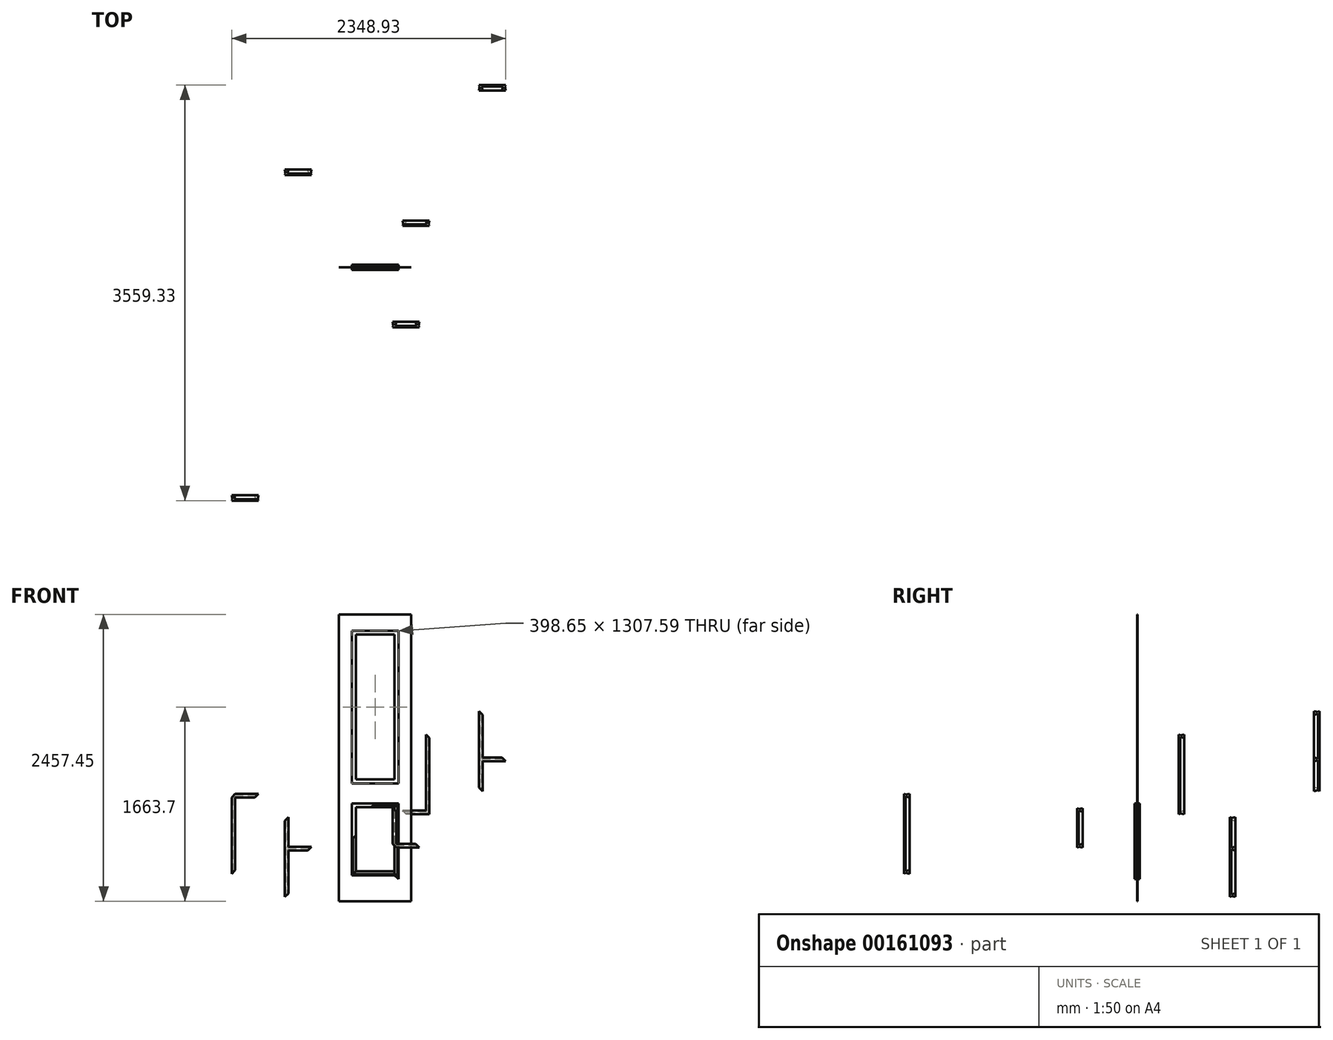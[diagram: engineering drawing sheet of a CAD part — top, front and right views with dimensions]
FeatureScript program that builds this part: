
annotation { "Feature Type Name" : "Feature", "Feature Type Description" : "" }
export const myFeature = defineFeature(function(context is Context, id is Id, definition is map)
    precondition{}
    {
        {
            var Q0;
            Q0=qCreatedBy(makeId("Front.planeOp"),FACE);
            var sketch = newSketch(context, id + "F0", { "sketchPlane" : qUnion([Q0])});
            skLineSegment(sketch, "E0.bottom", {"start": v(0, 0) * mm, "end": v(619.12, 0) * mm});
            skLineSegment(sketch, "E0.top", {"start": v(0, 2457.45) * mm, "end": v(619.12, 2457.45) * mm});
            skLineSegment(sketch, "E0.left", {"start": v(0, 0) * mm, "end": v(0, 2457.45) * mm});
            skLineSegment(sketch, "E0.right", {"start": v(619.12, 0) * mm, "end": v(619.12, 2457.45) * mm});
            skLineSegment(sketch, "E1.bottom", {"start": v(508.89, 2317.5) * mm, "end": v(110.24, 2317.5) * mm});
            skLineSegment(sketch, "E1.top", {"start": v(508.89, 1009.9) * mm, "end": v(110.24, 1009.9) * mm});
            skLineSegment(sketch, "E1.left", {"start": v(508.89, 2317.5) * mm, "end": v(508.89, 1009.9) * mm});
            skLineSegment(sketch, "E1.right", {"start": v(110.24, 2317.5) * mm, "end": v(110.24, 1009.9) * mm});
            skLineSegment(sketch, "E2.bottom", {"start": v(110.24, 837.7) * mm, "end": v(508.89, 837.7) * mm});
            skLineSegment(sketch, "E2.top", {"start": v(110.24, 222.5) * mm, "end": v(508.89, 222.5) * mm});
            skLineSegment(sketch, "E2.left", {"start": v(110.24, 837.7) * mm, "end": v(110.24, 222.5) * mm});
            skLineSegment(sketch, "E2.right", {"start": v(508.89, 837.7) * mm, "end": v(508.89, 222.5) * mm});
            skSolve(sketch);
        }
        {
            var Q0;
            Q0=qSketchRegion(id+"F0",true);
            extrude(context, id + "F1", {"entities" : qUnion([Q0]), "depth" : ((1 + 3 / 4) / 2) * mm, "hasSecondDirection" : true, "secondDirectionOppositeDirection" : true, "secondDirectionDepth" : ((1 + 3 / 4) / 2) * mm});
        }
        {
            var Q0;
            Q0=makeQuery(id+"F1.opExtrude","SWEPT_FACE",FACE,{"disambiguationData":[OSD([sQuery(id+"F0.wireOp",EDGE,"E2.top")])]});
            var sketch = newSketch(context, id + "F2", { "sketchPlane" : qUnion([Q0])});
            skLineSegment(sketch, "E3.0", {"start": v(110.24, 22.23) * mm, "end": v(508.89, 22.23) * mm});
            skLineSegment(sketch, "E4.0", {"start": v(110.24, -22.23) * mm, "end": v(508.89, -22.23) * mm});
            skLineSegment(sketch, "E5", {"start": v(309.56, -22.23) * mm, "end": v(309.56, 22.23) * mm});
            skLineSegment(sketch, "E6.0", {"start": v(110.24, -22.23) * mm, "end": v(110.24, 22.23) * mm});
            skLineSegment(sketch, "E7", {"start": v(110.24, 0) * mm, "end": v(309.56, 0) * mm});
            skLineSegment(sketch, "E8", {"start": v(309.56, 0) * mm, "end": v(508.89, 0) * mm});
            skSolve(sketch);
        }
        {
            var Q0;
            Q0=makeQuery(id+"F1.opExtrude","SWEPT_FACE",FACE,{"disambiguationData":[OSD([sQuery(id+"F0.wireOp",EDGE,"E2.top")])]});
            var sketch = newSketch(context, id + "F3", { "sketchPlane" : qUnion([Q0])});
            skLineSegment(sketch, "E9.0", {"start": v(110.24, -22.23) * mm, "end": v(110.24, 22.23) * mm});
            skLineSegment(sketch, "E10", {"start": v(110.24, -22.23) * mm, "end": v(128.2, -11.3) * mm});
            skLineSegment(sketch, "E11", {"start": v(128.2, -11.3) * mm, "end": v(177.4, -22.23) * mm});
            skLineSegment(sketch, "E12.MirrorCS", {"start": v(128.2, 11.3) * mm, "end": v(177.4, 22.23) * mm});
            skLineSegment(sketch, "E13.MirrorCS", {"start": v(110.24, 22.23) * mm, "end": v(128.2, 11.3) * mm});
            skLineSegment(sketch, "E14", {"start": v(177.4, 22.23) * mm, "end": v(177.4, -22.23) * mm});
            skLineSegment(sketch, "E15.MirrorCS", {"start": v(508.89, -22.23) * mm, "end": v(508.89, 22.22) * mm});
            skLineSegment(sketch, "E16.MirrorCS", {"start": v(508.89, 22.22) * mm, "end": v(490.93, 11.3) * mm});
            skLineSegment(sketch, "E17.MirrorCS", {"start": v(490.93, 11.3) * mm, "end": v(441.72, 22.23) * mm});
            skLineSegment(sketch, "E18.MirrorCS", {"start": v(441.72, 22.23) * mm, "end": v(441.72, -22.23) * mm});
            skLineSegment(sketch, "E19.MirrorCS", {"start": v(490.93, -11.3) * mm, "end": v(441.72, -22.23) * mm});
            skLineSegment(sketch, "E20.MirrorCS", {"start": v(508.89, -22.22) * mm, "end": v(490.93, -11.3) * mm});
            skSolve(sketch);
        }
        {
            var Q0;
            Q0=qCreatedBy(makeId("Front.planeOp"),FACE);
            var sketch = newSketch(context, id + "F4", { "sketchPlane" : qUnion([Q0])});
            skPoint(sketch, "E21.0", {"position": v(110.24, 222.5) * mm});
            skLineSegment(sketch, "E22", {"start": v(110.24, 222.5) * mm, "end": v(135.64, 247.9) * mm});
            skPoint(sketch, "E23.0", {"position": v(309.56, 222.5) * mm});
            skLineSegment(sketch, "E24", {"start": v(110.24, 530.1) * mm, "end": v(508.89, 530.1) * mm});
            skLineSegment(sketch, "E25", {"start": v(309.56, 837.7) * mm, "end": v(309.56, 222.5) * mm});
            skLineSegment(sketch, "E26.MirrorCS", {"start": v(110.24, 837.7) * mm, "end": v(135.64, 812.3) * mm});
            skLineSegment(sketch, "E27.MirrorCS", {"start": v(508.89, 837.7) * mm, "end": v(483.49, 812.3) * mm});
            skLineSegment(sketch, "E28.MirrorCS", {"start": v(508.89, 222.5) * mm, "end": v(483.49, 247.9) * mm});
            skLineSegment(sketch, "E29", {"start": v(508.89, 837.7) * mm, "end": v(309.56, 837.7) * mm});
            skLineSegment(sketch, "E30", {"start": v(309.56, 837.7) * mm, "end": v(110.24, 837.7) * mm});
            skLineSegment(sketch, "E31", {"start": v(508.89, 222.5) * mm, "end": v(508.89, 530.1) * mm});
            skLineSegment(sketch, "E32", {"start": v(508.89, 530.1) * mm, "end": v(508.89, 837.7) * mm});
            skLineSegment(sketch, "E33", {"start": v(110.24, 837.7) * mm, "end": v(110.24, 530.1) * mm});
            skLineSegment(sketch, "E34", {"start": v(110.24, 530.1) * mm, "end": v(110.24, 222.5) * mm});
            skLineSegment(sketch, "E35", {"start": v(508.89, 1663.7) * mm, "end": v(110.24, 1663.7) * mm});
            skLineSegment(sketch, "E36", {"start": v(309.56, 2317.5) * mm, "end": v(309.56, 1009.9) * mm});
            skPoint(sketch, "E37.0", {"position": v(508.89, 2317.5) * mm});
            skPoint(sketch, "E38.0", {"position": v(110.24, 2317.5) * mm});
            skPoint(sketch, "E39.0", {"position": v(508.89, 1009.9) * mm});
            skPoint(sketch, "E40.0", {"position": v(110.24, 1009.9) * mm});
            skLineSegment(sketch, "E41", {"start": v(508.89, 2317.5) * mm, "end": v(508.89, 1663.7) * mm});
            skLineSegment(sketch, "E42", {"start": v(508.89, 1663.7) * mm, "end": v(508.89, 1009.9) * mm});
            skLineSegment(sketch, "E43", {"start": v(508.89, 1009.9) * mm, "end": v(309.56, 1009.9) * mm});
            skLineSegment(sketch, "E44", {"start": v(309.56, 1009.9) * mm, "end": v(110.24, 1009.9) * mm});
            skLineSegment(sketch, "E45", {"start": v(110.24, 1009.9) * mm, "end": v(110.24, 1663.7) * mm});
            skLineSegment(sketch, "E46", {"start": v(110.24, 1663.7) * mm, "end": v(110.24, 2317.5) * mm});
            skLineSegment(sketch, "E47", {"start": v(110.24, 2317.5) * mm, "end": v(309.56, 2317.5) * mm});
            skLineSegment(sketch, "E48", {"start": v(309.56, 2317.5) * mm, "end": v(508.89, 2317.5) * mm});
            skLineSegment(sketch, "E49", {"start": v(508.89, 2317.5) * mm, "end": v(483.49, 2292.1) * mm});
            skLineSegment(sketch, "E50.MirrorCS", {"start": v(110.24, 2317.5) * mm, "end": v(135.64, 2292.1) * mm});
            skLineSegment(sketch, "E51.MirrorCS", {"start": v(508.89, 1009.9) * mm, "end": v(483.49, 1035.3) * mm});
            skLineSegment(sketch, "E52.MirrorCS", {"start": v(110.24, 1009.9) * mm, "end": v(135.64, 1035.3) * mm});
            skSolve(sketch);
        }
        {
            var Q0;
            Q0=sQuery(id+"F4.wireOp",VERTEX,"E22.end");
            var Q1;
            Q1=sQuery(id+"F4.wireOp",VERTEX,"E21.0");
            var Q2;
            Q2=sQuery(id+"F3.wireOp",VERTEX,"E13.MirrorCS.start");
            cPlane(context, id + "F5", {"entities" : qUnion([Q0, Q1, Q2]), "cplaneType" : CPlaneType.THREE_POINT, "offset" : 0 * mm, "width" : 152.4 * mm, "height" : 152.4 * mm});
        }
        {
            var Q0;
            Q0=qCreatedBy(id+"F5.planeOp",FACE);
            var sketch = newSketch(context, id + "F6", { "sketchPlane" : qUnion([Q0])});
            skLineSegment(sketch, "E53.0", {"start": v(-22.22, 282.78) * mm, "end": v(22.23, 282.78) * mm});
            skLineSegment(sketch, "E54.0", {"start": v(-11.3, 247.98) * mm, "end": v(-22.22, 282.78) * mm});
            skLineSegment(sketch, "E55.0", {"start": v(-22.22, 235.28) * mm, "end": v(-11.3, 247.98) * mm});
            skLineSegment(sketch, "E56.0", {"start": v(22.23, 235.28) * mm, "end": v(-22.22, 235.28) * mm});
            skLineSegment(sketch, "E57.0", {"start": v(22.23, 235.28) * mm, "end": v(11.3, 247.98) * mm});
            skLineSegment(sketch, "E58.0", {"start": v(11.3, 247.98) * mm, "end": v(22.23, 282.78) * mm});
            skSolve(sketch);
        }
        {
            var Q0;
            Q0=sQuery(id+"F4.wireOp",VERTEX,"E28.MirrorCS.end");
            var Q1;
            Q1=sQuery(id+"F4.wireOp",VERTEX,"E28.MirrorCS.start");
            var Q2;
            Q2=sQuery(id+"F3.wireOp",VERTEX,"E16.MirrorCS.start");
            cPlane(context, id + "F7", {"entities" : qUnion([Q0, Q1, Q2]), "cplaneType" : CPlaneType.THREE_POINT, "offset" : 25.4 * mm, "width" : 152.4 * mm, "height" : 152.4 * mm});
        }
        {
            var Q0;
            Q0=qCreatedBy(id+"F7.planeOp",FACE);
            var sketch = newSketch(context, id + "F8", { "sketchPlane" : qUnion([Q0])});
            skLineSegment(sketch, "E59.0.0", {"start": v(22.23, 79.39) * mm, "end": v(-22.22, 79.39) * mm});
            skLineSegment(sketch, "E59.0.1", {"start": v(-22.22, 79.39) * mm, "end": v(-11.3, 79.39) * mm});
            skLineSegment(sketch, "E59.0.2", {"start": v(-11.3, 79.39) * mm, "end": v(-22.22, 79.39) * mm});
            skLineSegment(sketch, "E59.0.3", {"start": v(-22.22, 79.39) * mm, "end": v(22.23, 79.39) * mm});
            skLineSegment(sketch, "E59.0.4", {"start": v(22.23, 79.39) * mm, "end": v(11.3, 79.39) * mm});
            skLineSegment(sketch, "E59.0.5", {"start": v(11.3, 79.39) * mm, "end": v(22.23, 79.39) * mm});
            skLineSegment(sketch, "E60.0", {"start": v(-22.22, -202.5) * mm, "end": v(-11.3, -189.8) * mm});
            skLineSegment(sketch, "E61.0", {"start": v(-11.3, -189.8) * mm, "end": v(-22.22, -155) * mm});
            skLineSegment(sketch, "E62.0", {"start": v(-22.22, -155) * mm, "end": v(22.23, -155) * mm});
            skLineSegment(sketch, "E63.0", {"start": v(11.3, -189.8) * mm, "end": v(22.23, -155) * mm});
            skLineSegment(sketch, "E64.0", {"start": v(22.23, -202.5) * mm, "end": v(11.3, -189.8) * mm});
            skLineSegment(sketch, "E65.0", {"start": v(22.23, -202.5) * mm, "end": v(-22.22, -202.5) * mm});
            skSolve(sketch);
        }
        {
            var Q0;
            Q0=qSketchRegion(id+"F6",true);
            var Q1;
            Q1=qSketchRegion(id+"F8",true);
            var Q2;
            Q2=sQuery(id+"F4.wireOp",EDGE,"E34");
            sweep(context, id + "F9", {"operationType" : NewBodyOperationType.ADD, "profiles" : qUnion([Q0, Q1]), "path" : qUnion([Q2])});
        }
        {
            var Q0;
            Q0=sQuery(id+"F4.wireOp",VERTEX,"E29.start");
            var Q1;
            Q1=sQuery(id+"F4.wireOp",VERTEX,"E27.MirrorCS.end");
            var Q2;
            Q2=makeQuery(id+"F1.opExtrude","CAP_VERTEX",VERTEX,{"disambiguationData":[OSD([sQuery(id+"F0.wireOp",EDGE,"E2.bottom"),sQuery(id+"F0.wireOp",EDGE,"E2.right")])],"isStart":false});
            cPlane(context, id + "F10", {"entities" : qUnion([Q0, Q1, Q2]), "cplaneType" : CPlaneType.THREE_POINT, "offset" : 25.4 * mm, "width" : 152.4 * mm, "height" : 152.4 * mm});
        }
        {
            var Q0;
            Q0=makeQuery(id+"F1.opExtrude","CAP_VERTEX",VERTEX,{"disambiguationData":[OSD([sQuery(id+"F0.wireOp",EDGE,"E2.bottom"),sQuery(id+"F0.wireOp",EDGE,"E2.left")])],"isStart":false});
            var Q1;
            Q1=sQuery(id+"F4.wireOp",VERTEX,"E26.MirrorCS.start");
            var Q2;
            Q2=sQuery(id+"F4.wireOp",VERTEX,"E26.MirrorCS.end");
            cPlane(context, id + "F11", {"entities" : qUnion([Q0, Q1, Q2]), "cplaneType" : CPlaneType.THREE_POINT, "offset" : 25.4 * mm, "width" : 152.4 * mm, "height" : 152.4 * mm});
        }
        {
            var Q0;
            Q0=makeQuery(id+"F1.opExtrude","SWEPT_FACE",FACE,{"disambiguationData":[OSD([sQuery(id+"F0.wireOp",EDGE,"E2.bottom")])]});
            var sketch = newSketch(context, id + "F12", { "sketchPlane" : qUnion([Q0])});
            skLineSegment(sketch, "E66.0", {"start": v(508.89, 22.23) * mm, "end": v(508.89, -22.22) * mm});
            skLineSegment(sketch, "E67.0", {"start": v(508.89, 22.22) * mm, "end": v(490.93, 11.3) * mm});
            skLineSegment(sketch, "E68.0", {"start": v(490.93, 11.3) * mm, "end": v(441.72, 22.23) * mm});
            skLineSegment(sketch, "E69.0", {"start": v(441.72, -22.23) * mm, "end": v(441.72, 22.23) * mm});
            skLineSegment(sketch, "E70.0", {"start": v(490.93, -11.3) * mm, "end": v(441.72, -22.23) * mm});
            skLineSegment(sketch, "E71.0", {"start": v(508.89, -22.22) * mm, "end": v(490.93, -11.3) * mm});
            skLineSegment(sketch, "E72.0", {"start": v(177.4, -22.23) * mm, "end": v(177.4, 22.23) * mm});
            skLineSegment(sketch, "E73.0", {"start": v(128.2, 11.3) * mm, "end": v(177.4, 22.23) * mm});
            skLineSegment(sketch, "E74.0", {"start": v(110.24, 22.23) * mm, "end": v(128.2, 11.3) * mm});
            skLineSegment(sketch, "E75.0", {"start": v(110.24, 22.23) * mm, "end": v(110.24, -22.22) * mm});
            skLineSegment(sketch, "E76.0", {"start": v(110.24, -22.23) * mm, "end": v(128.2, -11.3) * mm});
            skLineSegment(sketch, "E77.0", {"start": v(128.2, -11.3) * mm, "end": v(177.4, -22.23) * mm});
            skSolve(sketch);
        }
        {
            var Q0;
            Q0=qCreatedBy(id+"F10.planeOp",FACE);
            var sketch = newSketch(context, id + "F13", { "sketchPlane" : qUnion([Q0])});
            skLineSegment(sketch, "E78.0", {"start": v(-22.23, 952.18) * mm, "end": v(22.22, 952.18) * mm});
            skLineSegment(sketch, "E79.0", {"start": v(-22.23, 952.18) * mm, "end": v(-11.3, 939.48) * mm});
            skLineSegment(sketch, "E80.0", {"start": v(-11.3, 939.48) * mm, "end": v(-22.23, 904.68) * mm});
            skLineSegment(sketch, "E81.0", {"start": v(22.22, 904.68) * mm, "end": v(-22.23, 904.68) * mm});
            skLineSegment(sketch, "E82.0", {"start": v(11.3, 939.48) * mm, "end": v(22.22, 904.68) * mm});
            skLineSegment(sketch, "E83.0", {"start": v(22.22, 952.18) * mm, "end": v(11.3, 939.48) * mm});
            skSolve(sketch);
        }
        {
            var Q0;
            Q0=qCreatedBy(id+"F11.planeOp",FACE);
            var sketch = newSketch(context, id + "F14", { "sketchPlane" : qUnion([Q0])});
            skLineSegment(sketch, "E84.0", {"start": v(-501.69, -11.3) * mm, "end": v(-466.9, -22.23) * mm});
            skLineSegment(sketch, "E85.0", {"start": v(-466.9, 22.22) * mm, "end": v(-466.9, -22.23) * mm});
            skLineSegment(sketch, "E86.0", {"start": v(-501.69, 11.3) * mm, "end": v(-466.9, 22.22) * mm});
            skLineSegment(sketch, "E87.0", {"start": v(-514.39, 22.22) * mm, "end": v(-501.69, 11.3) * mm});
            skLineSegment(sketch, "E88.0", {"start": v(-514.39, -22.23) * mm, "end": v(-501.69, -11.3) * mm});
            skLineSegment(sketch, "E89.0", {"start": v(-514.39, -22.23) * mm, "end": v(-514.39, 22.22) * mm});
            skSolve(sketch);
        }
        {
            var Q0;
            Q0=qSketchRegion(id+"F13",true);
            var Q1;
            Q1=qSketchRegion(id+"F14",true);
            var Q2;
            Q2=sQuery(id+"F4.wireOp",EDGE,"E32");
            sweep(context, id + "F15", {"operationType" : NewBodyOperationType.ADD, "profiles" : qUnion([Q0, Q1]), "path" : qUnion([Q2])});
        }
        {
            var Q0;
            Q0=qSketchRegion(id+"F13",true);
            var Q1;
            Q1=sQuery(id+"F4.wireOp",EDGE,"E29");
            sweep(context, id + "F16", {"operationType" : NewBodyOperationType.ADD, "profiles" : qUnion([Q0]), "path" : qUnion([Q1])});
        }
        {
            var Q0;
            Q0=qSketchRegion(id+"F14",true);
            var Q1;
            Q1=sQuery(id+"F4.wireOp",EDGE,"E30");
            sweep(context, id + "F17", {"operationType" : NewBodyOperationType.ADD, "profiles" : qUnion([Q0]), "path" : qUnion([Q1])});
        }
        {
            var Q0;
            Q0=qSketchRegion(id+"F8",true);
            var Q1;
            Q1=sQuery(id+"F2.wireOp",EDGE,"E8");
            sweep(context, id + "F18", {"operationType" : NewBodyOperationType.ADD, "profiles" : qUnion([Q0]), "path" : qUnion([Q1])});
        }
        {
            var Q0;
            Q0=qSketchRegion(id+"F6",true);
            var Q1;
            Q1=sQuery(id+"F2.wireOp",EDGE,"E7");
            sweep(context, id + "F19", {"operationType" : NewBodyOperationType.ADD, "profiles" : qUnion([Q0]), "path" : qUnion([Q1])});
        }
        {
            var Q0;
            Q0=makeQuery(id+"F1.opExtrude","SWEPT_FACE",FACE,{"disambiguationData":[OSD([sQuery(id+"F0.wireOp",EDGE,"E1.top")])]});
            var sketch = newSketch(context, id + "F20", { "sketchPlane" : qUnion([Q0])});
            skLineSegment(sketch, "E90.0", {"start": v(177.4, 22.23) * mm, "end": v(177.4, -22.23) * mm});
            skLineSegment(sketch, "E91.0", {"start": v(128.2, 11.3) * mm, "end": v(177.4, 22.23) * mm});
            skLineSegment(sketch, "E92.0", {"start": v(110.24, 22.23) * mm, "end": v(128.2, 11.3) * mm});
            skLineSegment(sketch, "E93.0", {"start": v(110.24, -22.23) * mm, "end": v(110.24, 22.22) * mm});
            skLineSegment(sketch, "E94.0", {"start": v(110.24, -22.23) * mm, "end": v(128.2, -11.3) * mm});
            skLineSegment(sketch, "E95.0", {"start": v(128.2, -11.3) * mm, "end": v(177.4, -22.23) * mm});
            skLineSegment(sketch, "E96.0", {"start": v(490.93, -11.3) * mm, "end": v(441.72, -22.23) * mm});
            skLineSegment(sketch, "E97.0", {"start": v(441.72, 22.23) * mm, "end": v(441.72, -22.23) * mm});
            skLineSegment(sketch, "E98.0", {"start": v(490.93, 11.3) * mm, "end": v(441.72, 22.23) * mm});
            skLineSegment(sketch, "E99.0", {"start": v(508.89, -22.22) * mm, "end": v(490.93, -11.3) * mm});
            skLineSegment(sketch, "E100.0", {"start": v(508.89, 22.22) * mm, "end": v(490.93, 11.3) * mm});
            skLineSegment(sketch, "E101.0", {"start": v(508.89, -22.23) * mm, "end": v(508.89, 22.22) * mm});
            skSolve(sketch);
        }
        {
            var Q0;
            Q0=makeQuery(id+"F1.opExtrude","CAP_VERTEX",VERTEX,{"disambiguationData":[OSD([sQuery(id+"F0.wireOp",EDGE,"E1.bottom"),sQuery(id+"F0.wireOp",EDGE,"E1.left")])],"isStart":true});
            var Q1;
            Q1=sQuery(id+"F4.wireOp",VERTEX,"E37.0");
            var Q2;
            Q2=sQuery(id+"F4.wireOp",VERTEX,"E49.end");
            cPlane(context, id + "F21", {"entities" : qUnion([Q0, Q1, Q2]), "cplaneType" : CPlaneType.THREE_POINT, "offset" : 25.4 * mm, "width" : 152.4 * mm, "height" : 152.4 * mm});
        }
        {
            var Q0;
            Q0=sQuery(id+"F4.wireOp",VERTEX,"E38.0");
            var Q1;
            Q1=sQuery(id+"F4.wireOp",VERTEX,"E50.MirrorCS.end");
            var Q2;
            Q2=makeQuery(id+"F1.opExtrude","CAP_VERTEX",VERTEX,{"disambiguationData":[OSD([sQuery(id+"F0.wireOp",EDGE,"E1.bottom"),sQuery(id+"F0.wireOp",EDGE,"E1.right")])],"isStart":true});
            cPlane(context, id + "F22", {"entities" : qUnion([Q0, Q1, Q2]), "cplaneType" : CPlaneType.THREE_POINT, "offset" : 25.4 * mm, "width" : 152.4 * mm, "height" : 152.4 * mm});
        }
        {
            var Q0;
            Q0=sQuery(id+"F4.wireOp",VERTEX,"E40.0");
            var Q1;
            Q1=sQuery(id+"F4.wireOp",VERTEX,"E52.MirrorCS.end");
            var Q2;
            Q2=sQuery(id+"F20.wireOp",VERTEX,"E93.0.end");
            cPlane(context, id + "F23", {"entities" : qUnion([Q0, Q1, Q2]), "cplaneType" : CPlaneType.THREE_POINT, "offset" : 25.4 * mm, "width" : 152.4 * mm, "height" : 152.4 * mm});
        }
        {
            var Q0;
            Q0=sQuery(id+"F4.wireOp",VERTEX,"E51.MirrorCS.end");
            var Q1;
            Q1=sQuery(id+"F4.wireOp",VERTEX,"E39.0");
            var Q2;
            Q2=sQuery(id+"F20.wireOp",VERTEX,"E101.0.end");
            cPlane(context, id + "F24", {"entities" : qUnion([Q0, Q1, Q2]), "cplaneType" : CPlaneType.THREE_POINT, "offset" : 25.4 * mm, "width" : 152.4 * mm, "height" : 152.4 * mm});
        }
        {
            var Q0;
            Q0=makeQuery(id+"F1.opExtrude","SWEPT_FACE",FACE,{"disambiguationData":[OSD([sQuery(id+"F0.wireOp",EDGE,"E1.bottom")])]});
            var sketch = newSketch(context, id + "F25", { "sketchPlane" : qUnion([Q0])});
            skLineSegment(sketch, "E102.0", {"start": v(110.24, 22.23) * mm, "end": v(128.2, 11.3) * mm});
            skLineSegment(sketch, "E103.0", {"start": v(128.2, 11.3) * mm, "end": v(177.4, 22.23) * mm});
            skLineSegment(sketch, "E104.0", {"start": v(177.4, -22.23) * mm, "end": v(177.4, 22.23) * mm});
            skLineSegment(sketch, "E105.0", {"start": v(128.2, -11.3) * mm, "end": v(177.4, -22.23) * mm});
            skLineSegment(sketch, "E106.0", {"start": v(110.24, -22.23) * mm, "end": v(128.2, -11.3) * mm});
            skLineSegment(sketch, "E107.0", {"start": v(110.24, 22.23) * mm, "end": v(110.24, -22.22) * mm});
            skLineSegment(sketch, "E108.0", {"start": v(508.89, 22.23) * mm, "end": v(508.89, -22.22) * mm});
            skLineSegment(sketch, "E109.0", {"start": v(508.89, -22.23) * mm, "end": v(490.93, -11.3) * mm});
            skLineSegment(sketch, "E110.0", {"start": v(490.93, -11.3) * mm, "end": v(441.72, -22.23) * mm});
            skLineSegment(sketch, "E111.0", {"start": v(441.72, -22.23) * mm, "end": v(441.72, 22.23) * mm});
            skLineSegment(sketch, "E112.0", {"start": v(490.93, 11.3) * mm, "end": v(441.72, 22.23) * mm});
            skLineSegment(sketch, "E113.0", {"start": v(508.89, 22.22) * mm, "end": v(490.93, 11.3) * mm});
            skSolve(sketch);
        }
        {
            var Q0;
            Q0=qCreatedBy(id+"F21.planeOp",FACE);
            var sketch = newSketch(context, id + "F26", { "sketchPlane" : qUnion([Q0])});
            skLineSegment(sketch, "E114.0", {"start": v(1951.06, 22.23) * mm, "end": v(1951.06, -22.23) * mm});
            skLineSegment(sketch, "E115.0", {"start": v(1985.86, 11.3) * mm, "end": v(1951.06, 22.23) * mm});
            skLineSegment(sketch, "E116.0", {"start": v(1985.86, -11.3) * mm, "end": v(1951.06, -22.23) * mm});
            skLineSegment(sketch, "E117.0", {"start": v(1998.56, -22.23) * mm, "end": v(1985.86, -11.3) * mm});
            skLineSegment(sketch, "E118.0", {"start": v(1998.56, 22.23) * mm, "end": v(1985.86, 11.3) * mm});
            skLineSegment(sketch, "E119.0", {"start": v(1998.56, -22.23) * mm, "end": v(1998.56, 22.22) * mm});
            skSolve(sketch);
        }
        {
            var Q0;
            Q0=qCreatedBy(id+"F22.planeOp",FACE);
            var sketch = newSketch(context, id + "F27", { "sketchPlane" : qUnion([Q0])});
            skLineSegment(sketch, "E120.0", {"start": v(-1513.27, -22.22) * mm, "end": v(-1513.27, 22.23) * mm});
            skLineSegment(sketch, "E121.0", {"start": v(-1548.07, 11.3) * mm, "end": v(-1513.27, 22.23) * mm});
            skLineSegment(sketch, "E122.0", {"start": v(-1548.07, -11.3) * mm, "end": v(-1513.27, -22.22) * mm});
            skLineSegment(sketch, "E123.0", {"start": v(-1560.77, -22.22) * mm, "end": v(-1548.07, -11.3) * mm});
            skLineSegment(sketch, "E124.0", {"start": v(-1560.77, 22.23) * mm, "end": v(-1548.07, 11.3) * mm});
            skLineSegment(sketch, "E125.0", {"start": v(-1560.77, 22.23) * mm, "end": v(-1560.77, -22.22) * mm});
            skSolve(sketch);
        }
        {
            var Q0;
            Q0=qCreatedBy(id+"F24.planeOp",FACE);
            var sketch = newSketch(context, id + "F28", { "sketchPlane" : qUnion([Q0])});
            skLineSegment(sketch, "E126.0", {"start": v(-401.77, -22.23) * mm, "end": v(-401.77, 22.22) * mm});
            skLineSegment(sketch, "E127.0", {"start": v(-366.97, -11.3) * mm, "end": v(-401.77, -22.23) * mm});
            skLineSegment(sketch, "E128.0", {"start": v(-354.27, -22.23) * mm, "end": v(-366.97, -11.3) * mm});
            skLineSegment(sketch, "E129.0", {"start": v(-354.27, 22.22) * mm, "end": v(-354.27, -22.23) * mm});
            skLineSegment(sketch, "E130.0", {"start": v(-354.27, 22.22) * mm, "end": v(-366.97, 11.3) * mm});
            skLineSegment(sketch, "E131.0", {"start": v(-366.97, 11.3) * mm, "end": v(-401.77, 22.22) * mm});
            skSolve(sketch);
        }
        {
            var Q0;
            Q0=qCreatedBy(id+"F23.planeOp",FACE);
            var sketch = newSketch(context, id + "F29", { "sketchPlane" : qUnion([Q0])});
            skLineSegment(sketch, "E132.0", {"start": v(792.06, 22.22) * mm, "end": v(792.06, -22.23) * mm});
            skLineSegment(sketch, "E133.0", {"start": v(792.06, -22.23) * mm, "end": v(804.76, -11.3) * mm});
            skLineSegment(sketch, "E134.0", {"start": v(804.76, -11.3) * mm, "end": v(839.56, -22.23) * mm});
            skLineSegment(sketch, "E135.0", {"start": v(839.56, -22.23) * mm, "end": v(839.56, 22.22) * mm});
            skLineSegment(sketch, "E136.0", {"start": v(804.76, 11.3) * mm, "end": v(839.56, 22.22) * mm});
            skLineSegment(sketch, "E137.0", {"start": v(792.06, 22.22) * mm, "end": v(804.76, 11.3) * mm});
            skSolve(sketch);
        }
        {
            var Q0;
            Q0=qSketchRegion(id+"F26",true);
            var Q1;
            Q1=qSketchRegion(id+"F27",true);
            var Q2;
            Q2=sQuery(id+"F4.wireOp",EDGE,"E41");
            sweep(context, id + "F30", {"operationType" : NewBodyOperationType.ADD, "profiles" : qUnion([Q0, Q1]), "path" : qUnion([Q2])});
        }
        {
            var Q0;
            Q0=qSketchRegion(id+"F28",true);
            var Q1;
            Q1=qSketchRegion(id+"F29",true);
            var Q2;
            Q2=sQuery(id+"F4.wireOp",EDGE,"E42");
            sweep(context, id + "F31", {"operationType" : NewBodyOperationType.ADD, "profiles" : qUnion([Q0, Q1]), "path" : qUnion([Q2])});
        }
        {
            var Q0;
            Q0=qSketchRegion(id+"F28",true);
            var Q1;
            Q1=qSketchRegion(id+"F26",true);
            var Q2;
            Q2=sQuery(id+"F4.wireOp",EDGE,"E43");
            sweep(context, id + "F32", {"operationType" : NewBodyOperationType.ADD, "profiles" : qUnion([Q0, Q1]), "path" : qUnion([Q2])});
        }
        {
            var Q0;
            Q0=qSketchRegion(id+"F27",true);
            var Q1;
            Q1=sQuery(id+"F4.wireOp",EDGE,"E47");
            sweep(context, id + "F33", {"operationType" : NewBodyOperationType.ADD, "profiles" : qUnion([Q0]), "path" : qUnion([Q1])});
        }
        {
            var Q0;
            Q0=qSketchRegion(id+"F29",true);
            var Q1;
            Q1=sQuery(id+"F4.wireOp",EDGE,"E44");
            sweep(context, id + "F34", {"operationType" : NewBodyOperationType.ADD, "profiles" : qUnion([Q0]), "path" : qUnion([Q1])});
        }
        {
            var Q0;
            Q0=qCreatedBy(makeId("Front.planeOp"),FACE);
            var sketch = newSketch(context, id + "F35", { "sketchPlane" : qUnion([Q0])});
            skLineSegment(sketch, "E138.0", {"start": v(475.3, 2283.9) * mm, "end": v(143.82, 2283.9) * mm});
            skLineSegment(sketch, "E139.0", {"start": v(143.82, 2283.9) * mm, "end": v(143.82, 1043.5) * mm});
            skLineSegment(sketch, "E140.0", {"start": v(475.3, 2283.9) * mm, "end": v(475.3, 1043.5) * mm});
            skLineSegment(sketch, "E141.0", {"start": v(475.3, 1043.5) * mm, "end": v(143.82, 1043.5) * mm});
            skLineSegment(sketch, "E142.0", {"start": v(475.3, 804.1) * mm, "end": v(143.82, 804.1) * mm});
            skLineSegment(sketch, "E143.0", {"start": v(475.3, 256.1) * mm, "end": v(475.3, 804.1) * mm});
            skLineSegment(sketch, "E144.0", {"start": v(475.3, 256.1) * mm, "end": v(143.82, 256.1) * mm});
            skLineSegment(sketch, "E145.0", {"start": v(143.82, 256.1) * mm, "end": v(143.82, 804.1) * mm});
            skSolve(sketch);
        }
        {
            var Q0;
            Q0=qSketchRegion(id+"F35",true);
            extrude(context, id + "F36", {"entities" : qUnion([Q0]), "operationType" : NewBodyOperationType.ADD, "depth" : ((1 + 3 / 4) / 2) * mm, "hasSecondDirection" : true, "secondDirectionOppositeDirection" : true, "secondDirectionDepth" : ((1 + 3 / 4) / 2) * mm});
        }
    });
